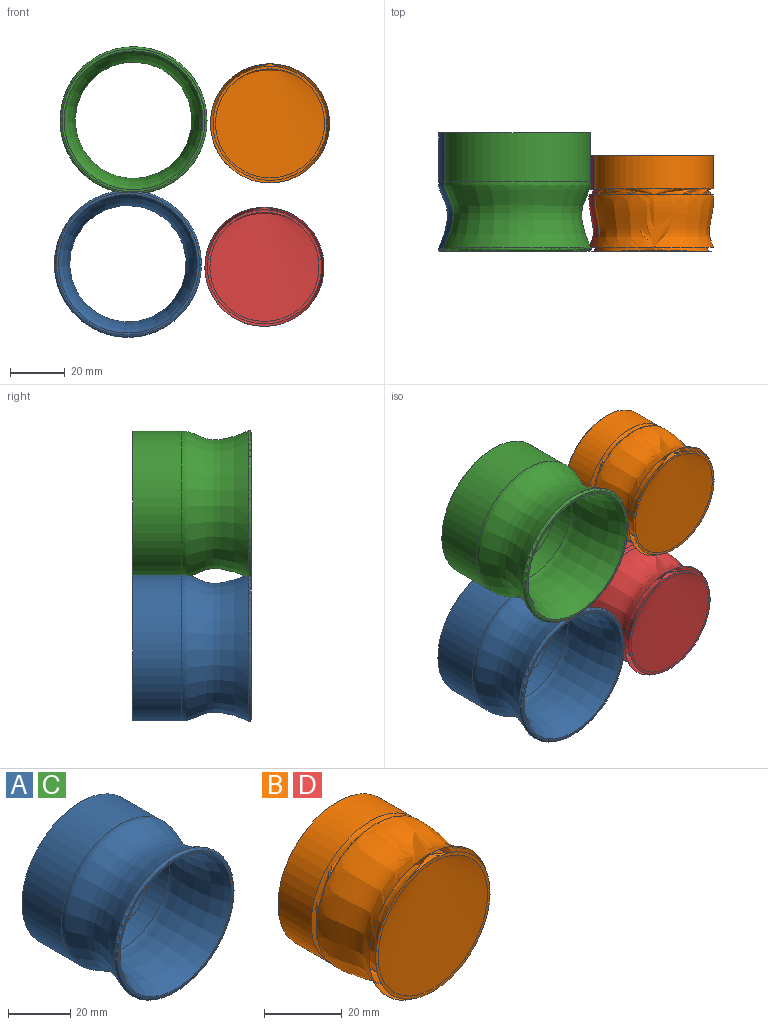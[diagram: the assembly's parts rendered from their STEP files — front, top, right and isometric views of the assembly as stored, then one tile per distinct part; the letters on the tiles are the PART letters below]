
ASSEMBLY  parts=4 mates=4
PART A: 49 faces, bbox 58.9x53.7x58.1 mm
  f0: torus R=24.25mm, axis (0,1,0), area 283.6mm2, adj f21,f47
  f1: plane 44.73x44.73mm, normal (0,1,0), area 122.4mm2, adj f8,f46
  f2: cone r=24.31mm half-angle=41.1deg, axis (0,1,0), area 166.3mm2, adj f3,f9,f10,f11,f12,f13,f14,f18
  f3: plane 53.26x53.26mm, normal (0,1,0), area 63.3mm2, adj f2,f4
  f4: cylinder r=26.63mm len=53.26mm, axis (0,1,0), area 2975.2mm2, adj f3,f5
  f5: revolved ~53.48x53.48mm, area 7936.2mm2, adj f4
  f6: plane 52.12x52.12mm, normal (0,-1,0), area 122.8mm2, adj f7,f48
  f7: revolved ~50.6x50.6mm, area 3472mm2, adj f6,f8
  f8: cylinder r=21.48mm len=42.95mm, axis (0,1,0), area 960.4mm2, adj f1,f7
  f9: cylinder r=25.66mm len=41.98mm, axis (0,1,0), area 81.7mm2, adj f2,f19,f23,f26,f35,f36,f43,f44
  f10: cylinder r=25.66mm len=36.45mm, axis (0,1,0), area 37.9mm2, adj f2,f18,f23,f27,f30,f38
  f11: cylinder r=25.66mm len=43.3mm, axis (0,1,0), area 77.8mm2, adj f2,f23,f24,f33,f34,f41
  f12: cylinder r=25.66mm len=33.42mm, axis (0,1,0), area 77.8mm2, adj f2,f23,f31,f32,f33,f40
  f13: cylinder r=25.66mm len=39.46mm, axis (0,1,0), area 77.8mm2, adj f2,f23,f30,f36,f37,f45
  f14: cylinder r=25.66mm len=36.08mm, axis (0,1,0), area 36.4mm2, adj f2,f23,f29,f31
  f15: cylinder r=25.66mm len=20.4mm, axis (0,1,0), area 24.7mm2, adj f19,f23,f25,f26
  f16: cylinder r=25.66mm len=26.35mm, axis (0,1,0), area 30.9mm2, adj f19,f23,f24,f25
  f17: cylinder r=25.66mm len=20.4mm, axis (0,1,0), area 24.7mm2, adj f18,f23,f28,f29
  f18: bspline ~23.74x17.84mm, area 26.5mm2, adj f2,f10,f17,f20,f27,f28,f29,f38
  f19: bspline ~22.07x17.3mm, area 22.6mm2, adj f2,f9,f15,f16,f24,f25,f26,f42
  f20: cylinder r=25.66mm len=26.35mm, axis (0,1,0), area 31.1mm2, adj f18,f22,f23,f27,f28
  f21: plane 48.75x48.75mm, normal (0,1,0), area 19.7mm2, adj f0,f23
  f22: torus R=24.38mm, axis (0,1,0), area 0mm2, adj f20,f23,f28
  f23: torus R=24.38mm, axis (0,1,0), area 211.2mm2, adj f9,f10,f11,f12,f13,f14,f15,f16
  f24: bspline ~41.11x28.91mm, area 165.3mm2, adj f2,f11,f16,f19,f23
  f25: bspline ~39.34x30.21mm, area 153.1mm2, adj f15,f16,f19,f23,f42
  f26: bspline ~46.1x20.62mm, area 152.3mm2, adj f9,f15,f19,f23,f43
  f27: bspline ~40.91x28.31mm, area 159.2mm2, adj f10,f18,f20,f23,f38
  f28: bspline ~39.34x30.21mm, area 160.1mm2, adj f17,f18,f20,f22,f23,f39
  f29: bspline ~46.1x20.62mm, area 163mm2, adj f2,f14,f17,f18,f23
  f30: bspline ~46.53x20.62mm, area 162.4mm2, adj f2,f10,f13,f23
  f31: bspline ~44.63x22.27mm, area 162.4mm2, adj f2,f12,f14,f23
  f32: bspline ~36.05x33.77mm, area 151.8mm2, adj f12,f23,f40
  f33: bspline ~43.35x24.66mm, area 162.4mm2, adj f2,f11,f12,f23
  f34: bspline ~46.53x20.62mm, area 151.8mm2, adj f11,f23,f41
  f35: bspline ~44.63x22.27mm, area 151.8mm2, adj f9,f23,f44
  f36: bspline ~36.05x33.77mm, area 169mm2, adj f2,f9,f13,f23
  f37: bspline ~43.35x24.66mm, area 151.8mm2, adj f13,f23,f45
  f38: bspline ~10.29x5.43mm, area 3.6mm2, adj f10,f18,f27
  f39: bspline ~12.46x1.63mm, area 0mm2, adj f18,f28
  f40: bspline ~10.11x3.08mm, area 0mm2, adj f12,f32
  f41: bspline ~8.38x7.35mm, area 0mm2, adj f11,f34
  f42: bspline ~12.46x1.63mm, area 0mm2, adj f19,f25
  f43: bspline ~9.39x5.59mm, area 3.4mm2, adj f9,f19,f26
  f44: bspline ~8.72x6.93mm, area 0mm2, adj f9,f35
  f45: bspline ~9.96x3.58mm, area 0mm2, adj f13,f37
  f46: cylinder r=22.36mm len=44.73mm, axis (0,1,0), area 820.9mm2, adj f1,f47
  f47: plane 45.92x45.92mm, normal (0,1,0), area 84.5mm2, adj f0,f46
  f48: torus R=26.06mm, axis (0,1,0), area 258.8mm2, adj f6
PART B: 51 faces, bbox 63.2x46.5x63.2 mm
  f0: plane 34.54x34.54mm, normal (0,1,0), area 94mm2, adj f1,f50
  f1: cylinder r=17.27mm len=34.54mm, axis (0,1,0), area 1102.6mm2, adj f0,f2
  f2: plane 35.58x35.58mm, normal (0,1,0), area 56.9mm2, adj f1,f3
  f3: cylinder r=17.79mm len=35.58mm, axis (0,1,0), area 333mm2, adj f2,f4
  f4: torus R=19.08mm, axis (0,-1,0), area 232.3mm2, adj f3,f5
  f5: plane 38.41x38.41mm, normal (0,1,0), area 15.5mm2, adj f4,f6
  f6: torus R=19.21mm, axis (0,-1,0), area 152.7mm2, adj f5,f7,f9,f29,f30,f31,f32,f33
  f7: bspline ~30.87x26.2mm, area 126.5mm2, adj f6,f8,f49
  f8: bspline ~10.41x2.3mm, area 0mm2, adj f7,f49
  f9: bspline ~37.5x18.27mm, area 145mm2, adj f6,f10,f29,f49
  f10: cone r=19.63mm half-angle=50.8deg, axis (0,1,0), area 149.5mm2, adj f9,f11,f12,f14,f16,f17,f19,f27
  f11: bspline ~12.58x2.58mm, area 0mm2, adj f10,f44
  f12: bspline ~17.81x9.87mm, area 10.4mm2, adj f10,f13,f41,f43,f44
  f13: bspline ~9.55x7mm, area 7.3mm2, adj f12,f41,f42,f43
  f14: bspline ~14.88x9.07mm, area 9.7mm2, adj f10,f15,f32,f33,f34,f35
  f15: plane 8.72x5.28mm, normal (0,1,0), area 3.3mm2, adj f14,f34,f35
  f16: bspline ~12.56x2.58mm, area 0mm2, adj f10,f32
  f17: bspline ~17.38x9.66mm, area 10.4mm2, adj f10,f18,f29,f31,f32
  f18: bspline ~9.55x7mm, area 7.3mm2, adj f17,f29,f30,f31
  f19: plane 43.14x43.14mm, normal (0,1,0), area 34.2mm2, adj f10,f20
  f20: cylinder r=21.57mm len=43.14mm, axis (0,1,0), area 1634.6mm2, adj f19,f21
  f21: torus R=46.97mm, axis (0,1,0), area 276.7mm2, adj f20,f22
  f22: revolved ~43.48x43.48mm, area 2591.3mm2, adj f21,f23
  f23: torus R=20.8mm, axis (0,1,0), area 276.1mm2, adj f22,f24
  f24: plane 41.59x41.59mm, normal (0,-1,0), area 115.9mm2, adj f23,f25
  f25: revolved ~39.78x39.78mm, area 1758.8mm2, adj f24,f26
  f26: torus R=21.46mm, axis (0,-1,0), area 187.2mm2, adj f25,f50
  f27: bspline ~14.87x9.06mm, area 11mm2, adj f10,f28,f44,f45,f46,f47
  f28: bspline ~9.71x6.03mm, area 4.3mm2, adj f27,f46,f47
  f29: cylinder r=20.5mm len=31.24mm, axis (0,-1,0), area 28mm2, adj f6,f9,f10,f17,f18,f30
  f30: bspline ~35.3x20.43mm, area 126.5mm2, adj f6,f18,f29,f31
  f31: cylinder r=20.5mm len=22.19mm, axis (0,-1,0), area 19.6mm2, adj f6,f17,f18,f30,f32
  f32: bspline ~30.87x26.2mm, area 150.4mm2, adj f6,f10,f14,f16,f17,f31,f33
  f33: cylinder r=20.5mm len=15.79mm, axis (0,-1,0), area 15.3mm2, adj f6,f14,f32,f34
  f34: bspline ~37.5x18.27mm, area 139.4mm2, adj f6,f14,f15,f33,f35
  f35: cylinder r=20.5mm len=29.03mm, axis (0,-1,0), area 26.8mm2, adj f6,f10,f14,f15,f34,f36
  f36: bspline ~35.3x20.43mm, area 145mm2, adj f6,f10,f35,f39
  f37: bspline ~30.87x26.2mm, area 126.5mm2, adj f6,f38,f39
  f38: bspline ~10.41x2.3mm, area 0mm2, adj f37,f39
  f39: cylinder r=20.5mm len=27.8mm, axis (0,-1,0), area 58mm2, adj f6,f10,f36,f37,f38,f40
  f40: bspline ~37.5x18.27mm, area 145mm2, adj f6,f10,f39,f41
  f41: cylinder r=20.5mm len=31.25mm, axis (0,-1,0), area 28mm2, adj f6,f10,f12,f13,f40,f42
  f42: bspline ~35.3x20.43mm, area 126.5mm2, adj f6,f13,f41,f43
  f43: cylinder r=20.5mm len=22.19mm, axis (0,-1,0), area 19.7mm2, adj f6,f12,f13,f42,f44
  f44: bspline ~30.87x26.2mm, area 150.4mm2, adj f6,f10,f11,f12,f27,f43,f45
  f45: cylinder r=20.5mm len=15.8mm, axis (0,-1,0), area 15.3mm2, adj f6,f27,f44,f46
  f46: bspline ~37.5x18.27mm, area 126.9mm2, adj f6,f27,f28,f45,f47
  f47: cylinder r=20.5mm len=29.03mm, axis (0,-1,0), area 30.4mm2, adj f6,f10,f27,f28,f46,f48
  f48: bspline ~35.3x20.43mm, area 145mm2, adj f6,f10,f47,f49
  f49: cylinder r=20.5mm len=27.8mm, axis (0,-1,0), area 58mm2, adj f6,f7,f8,f9,f10,f48
  f50: cylinder r=16.38mm len=32.77mm, axis (0,1,0), area 937.3mm2, adj f0,f26
PART C: same geometry as A
PART D: same geometry as B
PLACE A t=(-14.35,18.03,-18.26)mm fixed
PLACE B t=(37.46,14.1,32.95)mm
PLACE C t=(-12.32,18.03,34.07)mm
PLACE D t=(35.43,14.1,-19.38)mm fixed
MATE planar D.f3 <-> A.f0  axis (0,-1,0) through (35.43,-24,-19.38)mm
MATE planar A.f0 <-> C.f0  axis (0,-1,0) through (-14.35,-24,-18.26)mm
MATE planar D.f3 <-> B.f3  axis (0,-1,0) through (35.43,-24,-19.38)mm
MATE planar B.f3 <-> C.f0  axis (0,-1,0) through (37.46,-24,32.95)mm
